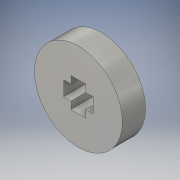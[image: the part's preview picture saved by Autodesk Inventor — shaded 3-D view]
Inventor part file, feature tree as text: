
AUTODESK INVENTOR PART (.ipt)
format: ipt  version: 2016 (Build 200138000, 138)  size: 123,904 bytes
history: native  units: in
note: dims shown in document units (in); Inventor stores cm internally (conversion verified against a paired STEP export)
features: extrude x2, sketch x2
ambient origin geometry x8: Origin, YZ Plane, XZ Plane, XY Plane, X Axis, Y Axis, Z Axis, Center Point
bodies: Solid1 (feature_tree)
feature tree (4):
  extrude  "Extrusion1"  Depth=0.374in TaperAngle=0.0deg
  extrude  "Extrusion2"  Depth=0.2362in
  sketch  "Sketch1"  dims[d0=1.4173in d1=0.374in d2=0.0in]
  sketch  "Sketch2"  dims[d18=0.4331in d19=0.0in d46=0.2362in d47=0.1181in d48=0.1181in d49=0.1181in d50=0.2362in d51=0.1181in d52=0.1181in d53=0.2362in d55=0.1181in d56=0.1181in d57=0.2362in d59=0.1181in d60=0.1181in]
